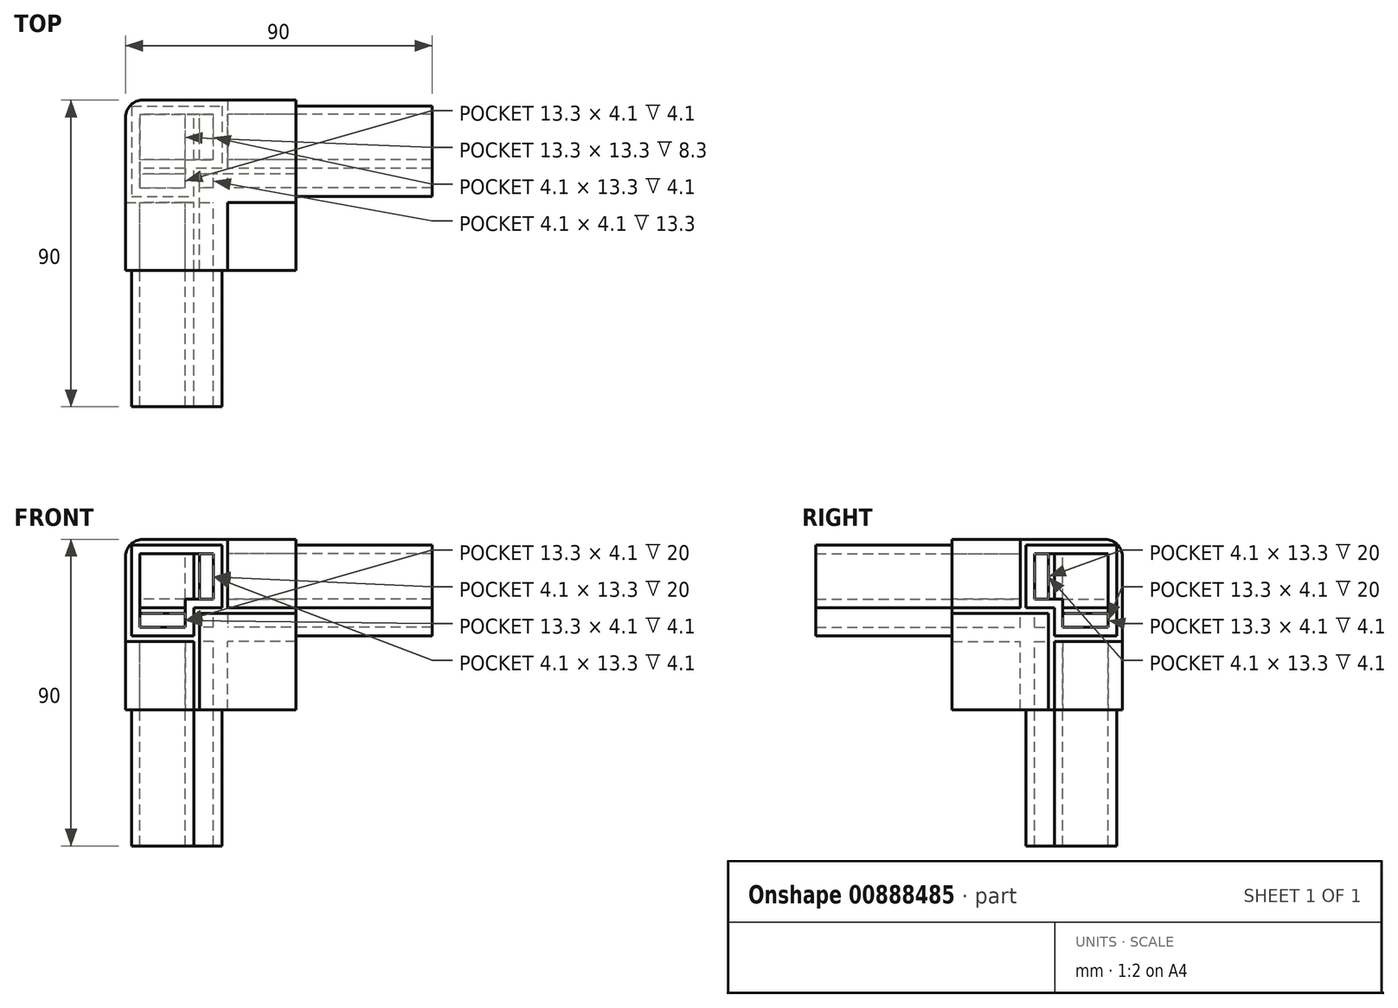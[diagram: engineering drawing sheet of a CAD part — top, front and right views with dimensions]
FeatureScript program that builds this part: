
annotation { "Feature Type Name" : "Feature", "Feature Type Description" : "" }
export const myFeature = defineFeature(function(context is Context, id is Id, definition is map)
    precondition{}
    {
        {
            var Q0;
            Q0=qCreatedBy(makeId("Front.planeOp"),FACE);
            var sketch = newSketch(context, id + "F0", { "sketchPlane" : qUnion([Q0])});
            skLineSegment(sketch, "E0.bottom", {"start": v(0, 0) * mm, "end": v(30, 0) * mm});
            skLineSegment(sketch, "E0.top", {"start": v(0, -30) * mm, "end": v(20, -30) * mm});
            skLineSegment(sketch, "E0.left", {"start": v(0, 0) * mm, "end": v(0, -30) * mm});
            skLineSegment(sketch, "E0.right", {"start": v(30, 0) * mm, "end": v(30, -20) * mm});
            skLineSegment(sketch, "E1.bottom", {"start": v(20, -20) * mm, "end": v(28.3, -20) * mm});
            skLineSegment(sketch, "E1.left", {"start": v(20, -20) * mm, "end": v(20, -28.3) * mm});
            skLineSegment(sketch, "E2", {"start": v(50, -20) * mm, "end": v(50, -21.7) * mm});
            skLineSegment(sketch, "E3", {"start": v(50, -21.7) * mm, "end": v(21.7, -21.7) * mm});
            skLineSegment(sketch, "E4", {"start": v(21.7, -21.7) * mm, "end": v(21.7, -50) * mm});
            skLineSegment(sketch, "E5", {"start": v(21.7, -50) * mm, "end": v(20, -50) * mm});
            skLineSegment(sketch, "E6.0", {"start": v(28.3, -1.7) * mm, "end": v(28.3, -20) * mm});
            skLineSegment(sketch, "E6.1", {"start": v(1.7, -1.7) * mm, "end": v(28.3, -1.7) * mm});
            skLineSegment(sketch, "E6.2", {"start": v(1.7, -1.7) * mm, "end": v(1.7, -28.3) * mm});
            skLineSegment(sketch, "E6.3", {"start": v(1.7, -28.3) * mm, "end": v(20, -28.3) * mm});
            skLineSegment(sketch, "E7.trimOffspring", {"start": v(30, -20) * mm, "end": v(50, -20) * mm});
            skLineSegment(sketch, "E8.trimOffspring", {"start": v(20, -30) * mm, "end": v(20, -50) * mm});
            skSolve(sketch);
        }
        {
            var Q0;
            Q0 = qSketchRegion(id + "F0", true);
            extrude(context, id + "F1", {"entities" : qUnion([Q0]), "depth" : 50 * mm, "offsetDistance" : 25 * mm});
        }
        {
            var Q0;
            Q0=qCreatedBy(makeId("Right.planeOp"),FACE);
            var sketch = newSketch(context, id + "F2", { "sketchPlane" : qUnion([Q0])});
            skLineSegment(sketch, "E9.bottom", {"start": v(0, 0) * mm, "end": v(30, 0) * mm});
            skLineSegment(sketch, "E9.top", {"start": v(0, -30) * mm, "end": v(20, -30) * mm});
            skLineSegment(sketch, "E9.left", {"start": v(0, 0) * mm, "end": v(0, -30) * mm});
            skLineSegment(sketch, "E9.right", {"start": v(30, 0) * mm, "end": v(30, -20) * mm});
            skLineSegment(sketch, "E10.bottom", {"start": v(20, -20) * mm, "end": v(28.3, -20) * mm});
            skLineSegment(sketch, "E10.left", {"start": v(20, -20) * mm, "end": v(20, -28.3) * mm});
            skLineSegment(sketch, "E11", {"start": v(50, -20) * mm, "end": v(50, -21.7) * mm});
            skLineSegment(sketch, "E12", {"start": v(50, -21.7) * mm, "end": v(21.7, -21.7) * mm});
            skLineSegment(sketch, "E13", {"start": v(21.7, -21.7) * mm, "end": v(21.7, -50) * mm});
            skLineSegment(sketch, "E14", {"start": v(21.7, -50) * mm, "end": v(20, -50) * mm});
            skLineSegment(sketch, "E15.0", {"start": v(28.3, -1.7) * mm, "end": v(28.3, -20) * mm});
            skLineSegment(sketch, "E15.1", {"start": v(1.7, -1.7) * mm, "end": v(28.3, -1.7) * mm});
            skLineSegment(sketch, "E15.2", {"start": v(1.7, -1.7) * mm, "end": v(1.7, -28.3) * mm});
            skLineSegment(sketch, "E15.3", {"start": v(1.7, -28.3) * mm, "end": v(20, -28.3) * mm});
            skLineSegment(sketch, "E16.trimOffspring", {"start": v(30, -20) * mm, "end": v(50, -20) * mm});
            skLineSegment(sketch, "E17.trimOffspring", {"start": v(20, -30) * mm, "end": v(20, -50) * mm});
            skLineSegment(sketch, "E18.MirrorCS", {"start": v(-50, -20) * mm, "end": v(-50, -21.7) * mm});
            skLineSegment(sketch, "E19.MirrorCS", {"start": v(-21.7, -50) * mm, "end": v(-20, -50) * mm});
            skLineSegment(sketch, "E20.MirrorCS", {"start": v(-1.7, -1.7) * mm, "end": v(-28.3, -1.7) * mm});
            skLineSegment(sketch, "E21.MirrorCS", {"start": v(0, 0) * mm, "end": v(-30, 0) * mm});
            skLineSegment(sketch, "E22.MirrorCS", {"start": v(-21.7, -21.7) * mm, "end": v(-21.7, -50) * mm});
            skLineSegment(sketch, "E23.MirrorCS", {"start": v(-20, -20) * mm, "end": v(-20, -28.3) * mm});
            skLineSegment(sketch, "E24.MirrorCS", {"start": v(-20, -20) * mm, "end": v(-28.3, -20) * mm});
            skLineSegment(sketch, "E25.MirrorCS", {"start": v(-1.7, -28.3) * mm, "end": v(-20, -28.3) * mm});
            skLineSegment(sketch, "E26.MirrorCS", {"start": v(-30, -20) * mm, "end": v(-50, -20) * mm});
            skLineSegment(sketch, "E27.MirrorCS", {"start": v(-30, 0) * mm, "end": v(-30, -20) * mm});
            skLineSegment(sketch, "E28.MirrorCS", {"start": v(0, -30) * mm, "end": v(-20, -30) * mm});
            skLineSegment(sketch, "E29.MirrorCS", {"start": v(-1.7, -1.7) * mm, "end": v(-1.7, -28.3) * mm});
            skLineSegment(sketch, "E30.MirrorCS", {"start": v(-28.3, -1.7) * mm, "end": v(-28.3, -20) * mm});
            skLineSegment(sketch, "E31.MirrorCS", {"start": v(-20, -30) * mm, "end": v(-20, -50) * mm});
            skLineSegment(sketch, "E32.MirrorCS", {"start": v(-50, -21.7) * mm, "end": v(-21.7, -21.7) * mm});
            skSolve(sketch);
        }
        {
            var Q0;
            Q0=makeQuery(id+"F2.imprint","IMPRINT",FACE,{"disambiguationData":[TD([[makeQuery(id+"F2.imprint","IMPRINT",EDGE,{"derivedFrom":sQuery(id+"F2.wireOp",EDGE,"E18.MirrorCS")}),1.0]])]});
            extrude(context, id + "F3", {"entities" : qUnion([Q0]), "operationType" : NewBodyOperationType.ADD, "depth" : 50 * mm, "offsetDistance" : 25 * mm});
        }
        {
            var Q0;
            Q0=makeQuery(id+"F3.boolean.opBoolean","MERGE",FACE,{"derivedFrom":[makeQuery(id+"F1.opExtrude","SWEPT_FACE",FACE,{"disambiguationData":[OSD([sQuery(id+"F0.wireOp",EDGE,"E0.bottom")])]}),makeQuery(id+"F3.opExtrude","SWEPT_FACE",FACE,{"disambiguationData":[OSD([sQuery(id+"F2.wireOp",EDGE,"E21.MirrorCS")])]})]});
            var sketch = newSketch(context, id + "F4", { "sketchPlane" : qUnion([Q0])});
            skLineSegment(sketch, "E33.bottom", {"start": v(0, 0) * mm, "end": v(30, 0) * mm});
            skLineSegment(sketch, "E33.top", {"start": v(0, -30) * mm, "end": v(20, -30) * mm});
            skLineSegment(sketch, "E33.left", {"start": v(0, 0) * mm, "end": v(0, -30) * mm});
            skLineSegment(sketch, "E33.right", {"start": v(30, 0) * mm, "end": v(30, -20) * mm});
            skLineSegment(sketch, "E34.bottom", {"start": v(20, -20) * mm, "end": v(28.3, -20) * mm});
            skLineSegment(sketch, "E34.left", {"start": v(20, -20) * mm, "end": v(20, -28.3) * mm});
            skLineSegment(sketch, "E35", {"start": v(50, -20) * mm, "end": v(50, -21.7) * mm});
            skLineSegment(sketch, "E36", {"start": v(50, -21.7) * mm, "end": v(21.7, -21.7) * mm});
            skLineSegment(sketch, "E37", {"start": v(21.7, -21.7) * mm, "end": v(21.7, -50) * mm});
            skLineSegment(sketch, "E38", {"start": v(21.7, -50) * mm, "end": v(20, -50) * mm});
            skLineSegment(sketch, "E39.0", {"start": v(28.3, -1.7) * mm, "end": v(28.3, -20) * mm});
            skLineSegment(sketch, "E39.1", {"start": v(1.7, -1.7) * mm, "end": v(28.3, -1.7) * mm});
            skLineSegment(sketch, "E39.2", {"start": v(1.7, -1.7) * mm, "end": v(1.7, -28.3) * mm});
            skLineSegment(sketch, "E39.3", {"start": v(1.7, -28.3) * mm, "end": v(20, -28.3) * mm});
            skLineSegment(sketch, "E40.trimOffspring", {"start": v(30, -20) * mm, "end": v(50, -20) * mm});
            skLineSegment(sketch, "E41.trimOffspring", {"start": v(20, -30) * mm, "end": v(20, -50) * mm});
            skSolve(sketch);
        }
        {
            var Q0;
            Q0 = qSketchRegion(id + "F4", true);
            extrude(context, id + "F5", {"entities" : qUnion([Q0]), "operationType" : NewBodyOperationType.ADD, "oppositeDirection" : true, "depth" : 50 * mm, "offsetDistance" : 25 * mm});
        }
        {
            var Q0;
            Q0=makeQuery(id+"F5.boolean.opBoolean","MERGE",FACE,{"derivedFrom":[makeQuery(id+"F3.boolean.opBoolean","MERGE",FACE,{"derivedFrom":[makeQuery(id+"F1.opExtrude","SWEPT_FACE",FACE,{"disambiguationData":[OSD([sQuery(id+"F0.wireOp",EDGE,"E0.left")])]}),makeQuery(id+"F3.opExtrude","CAP_FACE",FACE,{"disambiguationData":[OSD([sQuery(id+"F2.wireOp",EDGE,"E18.MirrorCS"),sQuery(id+"F2.wireOp",EDGE,"E19.MirrorCS"),sQuery(id+"F2.wireOp",EDGE,"E9.left"),sQuery(id+"F2.wireOp",EDGE,"E20.MirrorCS"),sQuery(id+"F2.wireOp",EDGE,"E21.MirrorCS"),sQuery(id+"F2.wireOp",EDGE,"E22.MirrorCS"),sQuery(id+"F2.wireOp",EDGE,"E23.MirrorCS"),sQuery(id+"F2.wireOp",EDGE,"E24.MirrorCS"),sQuery(id+"F2.wireOp",EDGE,"E25.MirrorCS"),sQuery(id+"F2.wireOp",EDGE,"E26.MirrorCS"),sQuery(id+"F2.wireOp",EDGE,"E27.MirrorCS"),sQuery(id+"F2.wireOp",EDGE,"E28.MirrorCS"),sQuery(id+"F2.wireOp",EDGE,"E29.MirrorCS"),sQuery(id+"F2.wireOp",EDGE,"E30.MirrorCS"),sQuery(id+"F2.wireOp",EDGE,"E31.MirrorCS"),sQuery(id+"F2.wireOp",EDGE,"E32.MirrorCS")])],"isStart":true})]}),makeQuery(id+"F5.opExtrude","SWEPT_FACE",FACE,{"disambiguationData":[OSD([sQuery(id+"F4.wireOp",EDGE,"E33.left")])]})]});
            var sketch = newSketch(context, id + "F6", { "sketchPlane" : qUnion([Q0])});
            skLineSegment(sketch, "E42.0", {"start": v(1.7, -1.7) * mm, "end": v(1.7, -20) * mm});
            skLineSegment(sketch, "E42.1", {"start": v(1.7, -1.7) * mm, "end": v(20, -1.7) * mm});
            skLineSegment(sketch, "E42.2", {"start": v(21.7, -1.7) * mm, "end": v(28.3, -1.7) * mm});
            skLineSegment(sketch, "E42.3", {"start": v(28.3, -1.7) * mm, "end": v(28.3, -20) * mm});
            skLineSegment(sketch, "E42.4", {"start": v(28.3, -20) * mm, "end": v(21.7, -20) * mm});
            skLineSegment(sketch, "E42.6", {"start": v(20, -21.7) * mm, "end": v(20, -28.3) * mm});
            skLineSegment(sketch, "E42.7", {"start": v(1.7, -28.3) * mm, "end": v(20, -28.3) * mm});
            skLineSegment(sketch, "E42.8", {"start": v(1.7, -21.7) * mm, "end": v(1.7, -28.3) * mm});
            skLineSegment(sketch, "E43", {"start": v(1.7, -20) * mm, "end": v(1.7, -21.7) * mm});
            skLineSegment(sketch, "E44", {"start": v(20, -20) * mm, "end": v(21.7, -20) * mm});
            skLineSegment(sketch, "E45", {"start": v(20, -20) * mm, "end": v(20, -21.7) * mm});
            skLineSegment(sketch, "E46", {"start": v(21.7, -1.7) * mm, "end": v(20, -1.7) * mm});
            skLineSegment(sketch, "E47.0", {"start": v(4.2, -4.2) * mm, "end": v(4.2, -20) * mm});
            skLineSegment(sketch, "E47.1", {"start": v(25.8, -17.5) * mm, "end": v(21.7, -17.5) * mm});
            skLineSegment(sketch, "E47.2", {"start": v(25.8, -4.2) * mm, "end": v(25.8, -17.5) * mm});
            skLineSegment(sketch, "E47.3", {"start": v(21.7, -4.2) * mm, "end": v(25.8, -4.2) * mm});
            skLineSegment(sketch, "E47.4", {"start": v(21.7, -4.2) * mm, "end": v(20, -4.2) * mm});
            skLineSegment(sketch, "E47.5", {"start": v(17.5, -17.5) * mm, "end": v(21.7, -17.5) * mm});
            skLineSegment(sketch, "E47.6", {"start": v(4.2, -4.2) * mm, "end": v(20, -4.2) * mm});
            skLineSegment(sketch, "E47.7", {"start": v(17.5, -17.5) * mm, "end": v(17.5, -21.7) * mm});
            skLineSegment(sketch, "E47.8", {"start": v(17.5, -21.7) * mm, "end": v(17.5, -25.8) * mm});
            skLineSegment(sketch, "E47.9", {"start": v(4.2, -25.8) * mm, "end": v(17.5, -25.8) * mm});
            skLineSegment(sketch, "E47.10", {"start": v(4.2, -21.7) * mm, "end": v(4.2, -25.8) * mm});
            skLineSegment(sketch, "E47.11", {"start": v(4.2, -20) * mm, "end": v(4.2, -21.7) * mm});
            skSolve(sketch);
        }
        {
            var Q0;
            Q0 = qSketchRegion(id + "F6", true);
            extrude(context, id + "F7", {"entities" : qUnion([Q0]), "operationType" : NewBodyOperationType.ADD, "oppositeDirection" : true, "depth" : 90 * mm, "offsetDistance" : 25 * mm});
        }
        {
            var Q0;
            Q0=makeQuery(id+"F5.boolean.opBoolean","MERGE",FACE,{"derivedFrom":[makeQuery(id+"F3.boolean.opBoolean","MERGE",FACE,{"derivedFrom":[makeQuery(id+"F1.opExtrude","CAP_FACE",FACE,{"disambiguationData":[OSD([sQuery(id+"F0.wireOp",EDGE,"E0.bottom"),sQuery(id+"F0.wireOp",EDGE,"E0.top"),sQuery(id+"F0.wireOp",EDGE,"E0.left"),sQuery(id+"F0.wireOp",EDGE,"E0.right"),sQuery(id+"F0.wireOp",EDGE,"E1.bottom"),sQuery(id+"F0.wireOp",EDGE,"E1.left"),sQuery(id+"F0.wireOp",EDGE,"E2"),sQuery(id+"F0.wireOp",EDGE,"E3"),sQuery(id+"F0.wireOp",EDGE,"E4"),sQuery(id+"F0.wireOp",EDGE,"E5"),sQuery(id+"F0.wireOp",EDGE,"E6.0"),sQuery(id+"F0.wireOp",EDGE,"E6.1"),sQuery(id+"F0.wireOp",EDGE,"E6.2"),sQuery(id+"F0.wireOp",EDGE,"E6.3"),sQuery(id+"F0.wireOp",EDGE,"E7.trimOffspring"),sQuery(id+"F0.wireOp",EDGE,"E8.trimOffspring")])],"isStart":true}),makeQuery(id+"F3.opExtrude","SWEPT_FACE",FACE,{"disambiguationData":[OSD([sQuery(id+"F2.wireOp",EDGE,"E9.left")])]})]}),makeQuery(id+"F5.opExtrude","SWEPT_FACE",FACE,{"disambiguationData":[OSD([sQuery(id+"F4.wireOp",EDGE,"E33.bottom")])]})]});
            var sketch = newSketch(context, id + "F8", { "sketchPlane" : qUnion([Q0])});
            skLineSegment(sketch, "E48.0", {"start": v(-1.7, -1.7) * mm, "end": v(-20, -1.7) * mm});
            skLineSegment(sketch, "E48.1", {"start": v(-1.7, -1.7) * mm, "end": v(-1.7, -20) * mm});
            skLineSegment(sketch, "E48.2", {"start": v(-1.7, -21.7) * mm, "end": v(-1.7, -28.3) * mm});
            skLineSegment(sketch, "E48.3", {"start": v(-1.7, -28.3) * mm, "end": v(-20, -28.3) * mm});
            skLineSegment(sketch, "E48.4", {"start": v(-20, -21.7) * mm, "end": v(-20, -28.3) * mm});
            skLineSegment(sketch, "E48.5", {"start": v(-21.7, -20) * mm, "end": v(-28.3, -20) * mm});
            skLineSegment(sketch, "E48.6", {"start": v(-28.3, -1.7) * mm, "end": v(-28.3, -20) * mm});
            skLineSegment(sketch, "E48.7", {"start": v(-21.7, -1.7) * mm, "end": v(-28.3, -1.7) * mm});
            skLineSegment(sketch, "E49", {"start": v(-20, -1.7) * mm, "end": v(-21.7, -1.7) * mm});
            skLineSegment(sketch, "E50", {"start": v(-21.7, -20) * mm, "end": v(-20, -20) * mm});
            skLineSegment(sketch, "E51", {"start": v(-20, -21.7) * mm, "end": v(-20, -20) * mm});
            skLineSegment(sketch, "E52", {"start": v(-1.7, -21.7) * mm, "end": v(-1.7, -20) * mm});
            skLineSegment(sketch, "E53.0", {"start": v(-4.2, -4.2) * mm, "end": v(-4.2, -20) * mm});
            skLineSegment(sketch, "E53.1", {"start": v(-21.7, -17.5) * mm, "end": v(-25.8, -17.5) * mm});
            skLineSegment(sketch, "E53.2", {"start": v(-25.8, -4.2) * mm, "end": v(-25.8, -17.5) * mm});
            skLineSegment(sketch, "E53.3", {"start": v(-21.7, -4.2) * mm, "end": v(-25.8, -4.2) * mm});
            skLineSegment(sketch, "E53.4", {"start": v(-20, -4.2) * mm, "end": v(-21.7, -4.2) * mm});
            skLineSegment(sketch, "E53.5", {"start": v(-21.7, -17.5) * mm, "end": v(-17.5, -17.5) * mm});
            skLineSegment(sketch, "E53.6", {"start": v(-4.2, -4.2) * mm, "end": v(-20, -4.2) * mm});
            skLineSegment(sketch, "E53.7", {"start": v(-17.5, -21.7) * mm, "end": v(-17.5, -17.5) * mm});
            skLineSegment(sketch, "E53.8", {"start": v(-17.5, -21.7) * mm, "end": v(-17.5, -25.8) * mm});
            skLineSegment(sketch, "E53.9", {"start": v(-4.2, -25.8) * mm, "end": v(-17.5, -25.8) * mm});
            skLineSegment(sketch, "E53.10", {"start": v(-4.2, -21.7) * mm, "end": v(-4.2, -25.8) * mm});
            skLineSegment(sketch, "E53.11", {"start": v(-4.2, -21.7) * mm, "end": v(-4.2, -20) * mm});
            skSolve(sketch);
        }
        {
            var Q0;
            Q0 = qSketchRegion(id + "F8", true);
            extrude(context, id + "F9", {"entities" : qUnion([Q0]), "operationType" : NewBodyOperationType.ADD, "oppositeDirection" : true, "depth" : 90 * mm, "offsetDistance" : 25 * mm});
        }
        {
            var Q0;
            Q0=makeQuery(id+"F3.boolean.opBoolean","MERGE",FACE,{"derivedFrom":[makeQuery(id+"F1.opExtrude","SWEPT_FACE",FACE,{"disambiguationData":[OSD([sQuery(id+"F0.wireOp",EDGE,"E0.bottom")])]}),makeQuery(id+"F3.opExtrude","SWEPT_FACE",FACE,{"disambiguationData":[OSD([sQuery(id+"F2.wireOp",EDGE,"E21.MirrorCS")])]})]});
            var sketch = newSketch(context, id + "F10", { "sketchPlane" : qUnion([Q0])});
            skLineSegment(sketch, "E54.0", {"start": v(1.7, -1.7) * mm, "end": v(1.7, -20) * mm});
            skLineSegment(sketch, "E54.1", {"start": v(1.7, -1.7) * mm, "end": v(20, -1.7) * mm});
            skLineSegment(sketch, "E54.3", {"start": v(21.7, -1.7) * mm, "end": v(28.3, -1.7) * mm});
            skLineSegment(sketch, "E54.4", {"start": v(28.3, -1.7) * mm, "end": v(28.3, -20) * mm});
            skLineSegment(sketch, "E54.5", {"start": v(28.3, -20) * mm, "end": v(21.7, -20) * mm});
            skLineSegment(sketch, "E54.6", {"start": v(20, -28.3) * mm, "end": v(20, -21.7) * mm});
            skLineSegment(sketch, "E54.7", {"start": v(1.7, -28.3) * mm, "end": v(20, -28.3) * mm});
            skLineSegment(sketch, "E54.8", {"start": v(1.7, -21.7) * mm, "end": v(1.7, -28.3) * mm});
            skLineSegment(sketch, "E55", {"start": v(1.7, -20) * mm, "end": v(1.7, -21.7) * mm});
            skLineSegment(sketch, "E56", {"start": v(20, -21.7) * mm, "end": v(20, -20) * mm});
            skLineSegment(sketch, "E57", {"start": v(20, -20) * mm, "end": v(21.7, -20) * mm});
            skLineSegment(sketch, "E58", {"start": v(21.7, -1.7) * mm, "end": v(20, -1.7) * mm});
            skLineSegment(sketch, "E59.0", {"start": v(4.2, -21.7) * mm, "end": v(4.2, -25.8) * mm});
            skLineSegment(sketch, "E59.1", {"start": v(25.8, -17.5) * mm, "end": v(21.7, -17.5) * mm});
            skLineSegment(sketch, "E59.2", {"start": v(17.5, -17.5) * mm, "end": v(21.7, -17.5) * mm});
            skLineSegment(sketch, "E59.3", {"start": v(17.5, -21.7) * mm, "end": v(17.5, -17.5) * mm});
            skLineSegment(sketch, "E59.4", {"start": v(17.5, -25.8) * mm, "end": v(17.5, -21.7) * mm});
            skLineSegment(sketch, "E59.5", {"start": v(25.8, -4.2) * mm, "end": v(25.8, -17.5) * mm});
            skLineSegment(sketch, "E59.6", {"start": v(4.2, -25.8) * mm, "end": v(17.5, -25.8) * mm});
            skLineSegment(sketch, "E59.7", {"start": v(21.7, -4.2) * mm, "end": v(25.8, -4.2) * mm});
            skLineSegment(sketch, "E59.8", {"start": v(21.7, -4.2) * mm, "end": v(20, -4.2) * mm});
            skLineSegment(sketch, "E59.9", {"start": v(4.2, -4.2) * mm, "end": v(20, -4.2) * mm});
            skLineSegment(sketch, "E59.10", {"start": v(4.2, -4.2) * mm, "end": v(4.2, -20) * mm});
            skLineSegment(sketch, "E59.11", {"start": v(4.2, -20) * mm, "end": v(4.2, -21.7) * mm});
            skSolve(sketch);
        }
        {
            var Q0;
            Q0 = qSketchRegion(id + "F10", true);
            extrude(context, id + "F11", {"entities" : qUnion([Q0]), "operationType" : NewBodyOperationType.ADD, "oppositeDirection" : true, "depth" : 90 * mm, "offsetDistance" : 25 * mm});
        }
        {
            var Q0;
            Q0=makeQuery(id+"F1.opExtrude","SWEPT_EDGE",EDGE,{"disambiguationData":[OSD([sQuery(id+"F0.wireOp",EDGE,"E0.bottom"),sQuery(id+"F0.wireOp",EDGE,"E0.left")])]});
            var Q1;
            Q1=makeQuery(id+"F5.boolean.opBoolean","MERGE",EDGE,{"derivedFrom":[makeQuery(id+"F1.opExtrude","CAP_EDGE",EDGE,{"disambiguationData":[OSD([sQuery(id+"F0.wireOp",EDGE,"E0.left")])],"isStart":true}),makeQuery(id+"F5.opExtrude","SWEPT_EDGE",EDGE,{"disambiguationData":[OSD([sQuery(id+"F4.wireOp",EDGE,"E33.bottom"),sQuery(id+"F4.wireOp",EDGE,"E33.left")])]})]});
            var Q2;
            Q2=makeQuery(id+"F3.boolean.opBoolean","MERGE",EDGE,{"derivedFrom":[makeQuery(id+"F1.opExtrude","CAP_EDGE",EDGE,{"disambiguationData":[OSD([sQuery(id+"F0.wireOp",EDGE,"E0.bottom")])],"isStart":true}),makeQuery(id+"F3.opExtrude","SWEPT_EDGE",EDGE,{"disambiguationData":[OSD([sQuery(id+"F2.wireOp",EDGE,"E9.bottom"),sQuery(id+"F2.wireOp",EDGE,"E9.left"),sQuery(id+"F2.wireOp",EDGE,"E21.MirrorCS")])]})]});
            fillet(context, id + "F12", {"entities" : qUnion([Q0, Q1, Q2]), "radius" : 5 * mm, "tangentPropagation" : true, "allowEdgeOverflow" : false});
        }
    });
